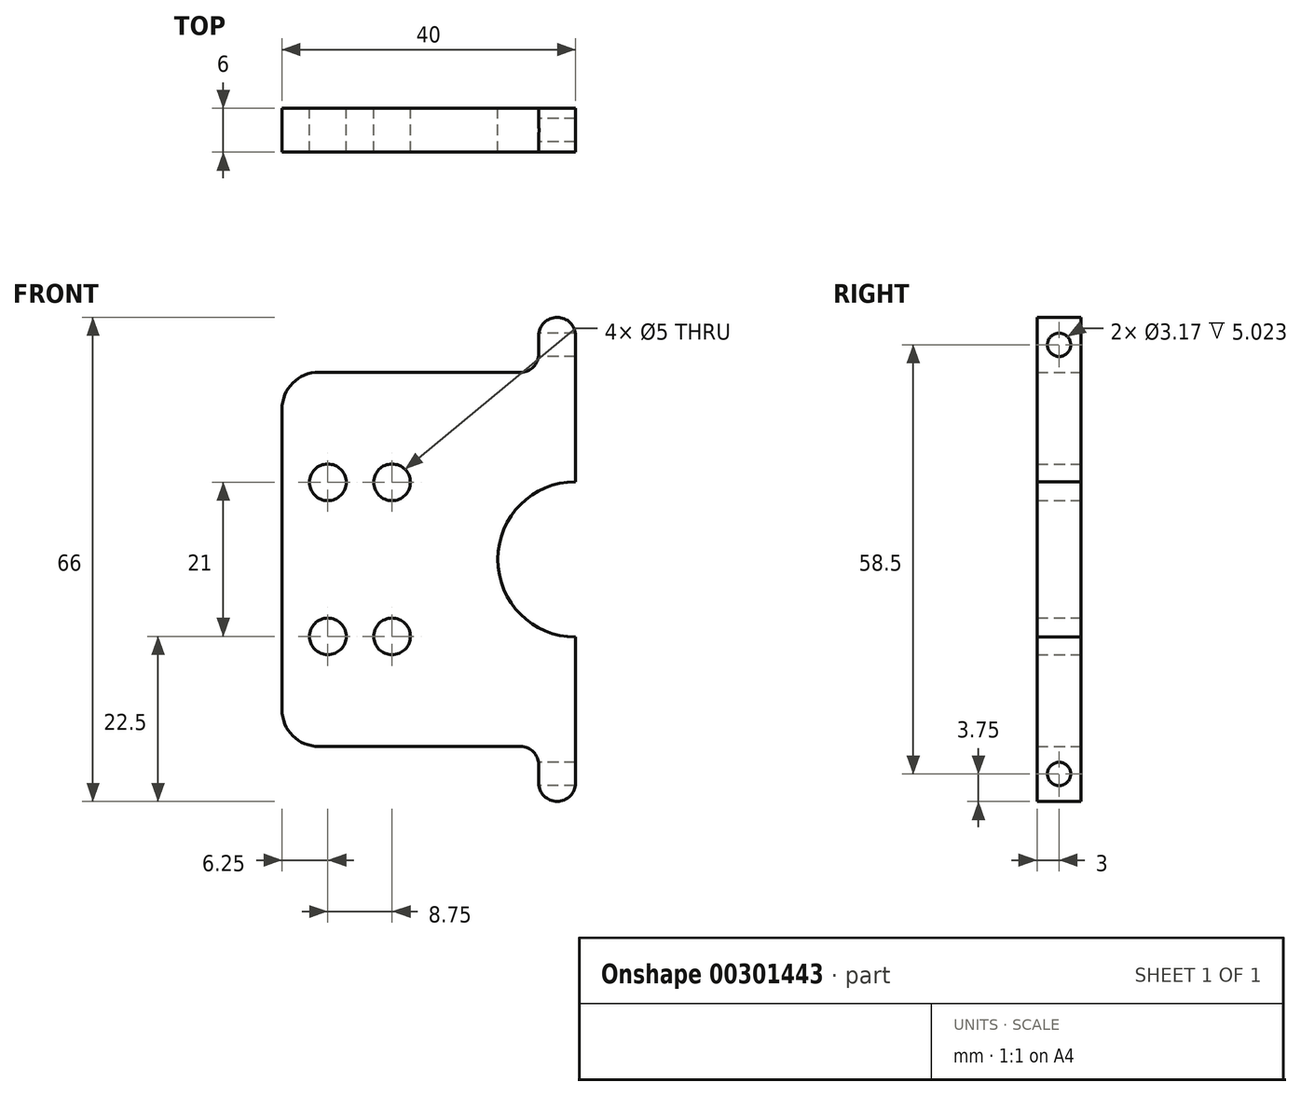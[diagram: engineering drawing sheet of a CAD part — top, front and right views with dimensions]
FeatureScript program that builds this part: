
annotation { "Feature Type Name" : "Feature", "Feature Type Description" : "" }
export const myFeature = defineFeature(function(context is Context, id is Id, definition is map)
    precondition{}
    {
        {
            var Q0;
            Q0=qCreatedBy(makeId("Front.planeOp"),FACE);
            var sketch = newSketch(context, id + "F0", { "sketchPlane" : qUnion([Q0])});
            skPoint(sketch, "E0", {"position": v(-29.1, 8.76) * mm});
            skCircle(sketch, "E1", {"center": v(-22.85, 8.76) * mm, "radius": 2.5 * mm});
            skCircle(sketch, "E2", {"center": v(-14.1, 8.76) * mm, "radius": 2.5 * mm});
            skCircle(sketch, "E3.MirrorC", {"center": v(-22.85, -12.24) * mm, "radius": 2.5 * mm});
            skCircle(sketch, "E4.MirrorC", {"center": v(-14.1, -12.24) * mm, "radius": 2.5 * mm});
            skLineSegment(sketch, "E5", {"start": v(-29.1, 8.76) * mm, "end": v(-14.1, 8.76) * mm});
            skLineSegment(sketch, "E6", {"start": v(-14.1, -12.24) * mm, "end": v(-29.1, -12.24) * mm});
            skPoint(sketch, "E7", {"position": v(5.9, 23.76) * mm});
            skPoint(sketch, "E8.MirrorP", {"position": v(5.9, -27.24) * mm});
            skPoint(sketch, "E9", {"position": v(10.9, 31.26) * mm});
            skLineSegment(sketch, "E10", {"start": v(10.9, -27.24) * mm, "end": v(10.9, -34.74) * mm});
            skLineSegment(sketch, "E11", {"start": v(10.9, 23.76) * mm, "end": v(10.9, 8.85) * mm});
            skArc(sketch, "E12", {"start": v(10.9, 8.85) * mm, "mid": v(0.31, -1.74) * mm, "end": v(10.9, -12.33) * mm});
            skLineSegment(sketch, "E13", {"start": v(10.9, -12.33) * mm, "end": v(10.9, -27.24) * mm});
            skLineSegment(sketch, "E14", {"start": v(10.9, 23.76) * mm, "end": v(10.9, 27.5) * mm});
            skLineSegment(sketch, "E15", {"start": v(10.9, -32.24) * mm, "end": v(10.9, -30.99) * mm});
            skLineSegment(sketch, "E16", {"start": v(3.4, -27.24) * mm, "end": v(3.4, -27.24) * mm});
            skArc(sketch, "E17.filletArc", {"start": v(5.9, -29.74) * mm, "mid": v(5.17, -27.97) * mm, "end": v(3.4, -27.24) * mm});
            skLineSegment(sketch, "E18", {"start": v(5.9, -32.24) * mm, "end": v(5.9, -32.24) * mm});
            skLineSegment(sketch, "E19", {"start": v(8.4, -34.74) * mm, "end": v(8.4, -34.74) * mm});
            skLineSegment(sketch, "E20", {"start": v(10.9, -34.74) * mm, "end": v(10.9, -32.24) * mm});
            skLineSegment(sketch, "E21", {"start": v(5.9, -29.74) * mm, "end": v(5.9, -32.24) * mm});
            skPoint(sketch, "E22.visualSharp", {"position": v(5.9, -34.74) * mm});
            skArc(sketch, "E22.filletArc", {"start": v(5.9, -32.24) * mm, "mid": v(6.63, -34) * mm, "end": v(8.4, -34.74) * mm});
            skPoint(sketch, "E23.visualSharp", {"position": v(10.9, -34.74) * mm});
            skArc(sketch, "E23.filletArc", {"start": v(8.4, -34.74) * mm, "mid": v(10.17, -34) * mm, "end": v(10.9, -32.24) * mm});
            skArc(sketch, "E24.MirrorCS", {"start": v(5.9, 26.26) * mm, "mid": v(5.17, 24.5) * mm, "end": v(3.4, 23.76) * mm});
            skLineSegment(sketch, "E25.MirrorCS", {"start": v(5.9, 26.26) * mm, "end": v(5.9, 28.76) * mm});
            skArc(sketch, "E26.MirrorCS", {"start": v(5.9, 28.76) * mm, "mid": v(6.63, 30.53) * mm, "end": v(8.4, 31.26) * mm});
            skArc(sketch, "E27.MirrorCS", {"start": v(8.4, 31.26) * mm, "mid": v(10.17, 30.53) * mm, "end": v(10.9, 28.76) * mm});
            skLineSegment(sketch, "E28.MirrorCS", {"start": v(10.9, 28.76) * mm, "end": v(10.9, 27.5) * mm});
            skLineSegment(sketch, "E29", {"start": v(-24.1, 23.76) * mm, "end": v(3.4, 23.76) * mm});
            skPoint(sketch, "E30.visualSharp", {"position": v(-29.1, 23.76) * mm});
            skArc(sketch, "E30.filletArc", {"start": v(-24.1, 23.76) * mm, "mid": v(-27.64, 22.3) * mm, "end": v(-29.1, 18.76) * mm});
            skArc(sketch, "E31.MirrorCS", {"start": v(-24.1, -27.24) * mm, "mid": v(-27.64, -25.78) * mm, "end": v(-29.1, -22.24) * mm});
            skLineSegment(sketch, "E32", {"start": v(-24.1, -27.24) * mm, "end": v(3.4, -27.24) * mm});
            skLineSegment(sketch, "E33", {"start": v(-29.1, -22.24) * mm, "end": v(-29.1, 18.76) * mm});
            skSolve(sketch);
        }
        {
            var Q0;
            Q0=makeQuery(id+"F0.imprint","IMPRINT",FACE,{"disambiguationData":[TD([[makeQuery(id+"F0.imprint","IMPRINT",EDGE,{"derivedFrom":sQuery(id+"F0.wireOp",EDGE,"E2")}),-1.0]])]});
            extrude(context, id + "F1", {"entities" : qUnion([Q0]), "endBound" : BoundingType.SYMMETRIC, "depth" : 6 * mm});
        }
        {
            var Q0;
            Q0=qCreatedBy(makeId("Right.planeOp"),FACE);
            var sketch = newSketch(context, id + "F2", { "sketchPlane" : qUnion([Q0])});
            skCircle(sketch, "E34", {"center": v(0, 27.5) * mm, "radius": 1.59 * mm});
            skCircle(sketch, "E35", {"center": v(0, -30.99) * mm, "radius": 1.59 * mm});
            skSolve(sketch);
        }
        {
            var Q0;
            Q0=qSketchRegion(id+"F2",true);
            extrude(context, id + "F3", {"entities" : qUnion([Q0]), "operationType" : NewBodyOperationType.REMOVE, "endBound" : BoundingType.THROUGH_ALL, "depth" : 25 * mm});
        }
    });
